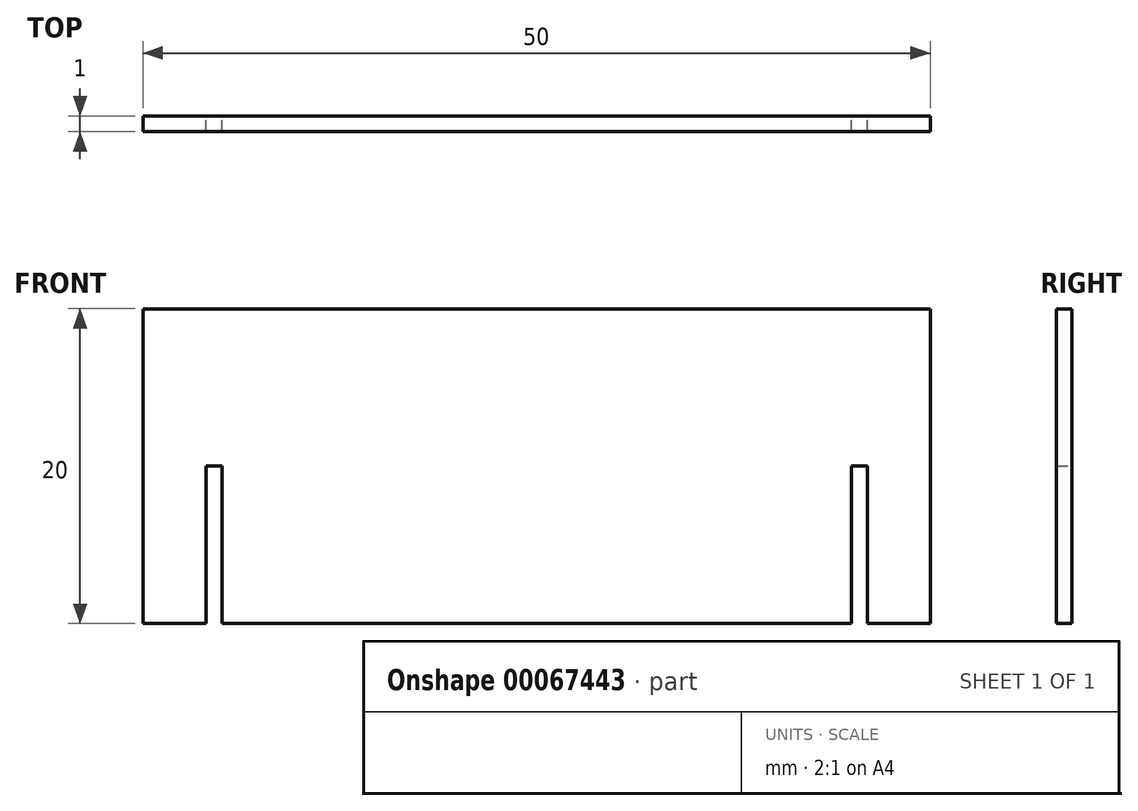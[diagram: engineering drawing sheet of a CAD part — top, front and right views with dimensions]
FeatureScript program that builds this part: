
annotation { "Feature Type Name" : "Feature", "Feature Type Description" : "" }
export const myFeature = defineFeature(function(context is Context, id is Id, definition is map)
    precondition{}
    {
        {
            var Q0;
            Q0=qCreatedBy(makeId("Front.planeOp"),FACE);
            var sketch = newSketch(context, id + "F0", { "sketchPlane" : qUnion([Q0])});
            skLineSegment(sketch, "E0.top", {"start": v(-22.86, -11.78) * mm, "end": v(-18.86, -11.78) * mm});
            skLineSegment(sketch, "E0.left", {"start": v(-22.86, 8.22) * mm, "end": v(-22.86, -11.78) * mm});
            skLineSegment(sketch, "E0.right", {"start": v(27.14, 8.22) * mm, "end": v(27.14, -11.78) * mm});
            skLineSegment(sketch, "E1", {"start": v(-22.86, 8.22) * mm, "end": v(27.14, 8.22) * mm});
            skLineSegment(sketch, "E2.top", {"start": v(-18.86, -1.78) * mm, "end": v(-17.86, -1.78) * mm});
            skLineSegment(sketch, "E2.left", {"start": v(-18.86, -11.78) * mm, "end": v(-18.86, -1.78) * mm});
            skLineSegment(sketch, "E2.right", {"start": v(-17.86, -11.78) * mm, "end": v(-17.86, -1.78) * mm});
            skLineSegment(sketch, "E3.top", {"start": v(23.14, -1.78) * mm, "end": v(22.14, -1.78) * mm});
            skLineSegment(sketch, "E3.left", {"start": v(23.14, -11.78) * mm, "end": v(23.14, -1.78) * mm});
            skLineSegment(sketch, "E3.right", {"start": v(22.14, -11.78) * mm, "end": v(22.14, -1.78) * mm});
            skLineSegment(sketch, "E4.trimOffspring", {"start": v(23.14, -11.78) * mm, "end": v(27.14, -11.78) * mm});
            skLineSegment(sketch, "E5", {"start": v(-17.86, -11.78) * mm, "end": v(22.14, -11.78) * mm});
            skSolve(sketch);
        }
        {
            var Q0;
            Q0 = qSketchRegion(id + "F0", true);
            extrude(context, id + "F1", {"entities" : qUnion([Q0]), "depth" : 1 * mm});
        }
    });
